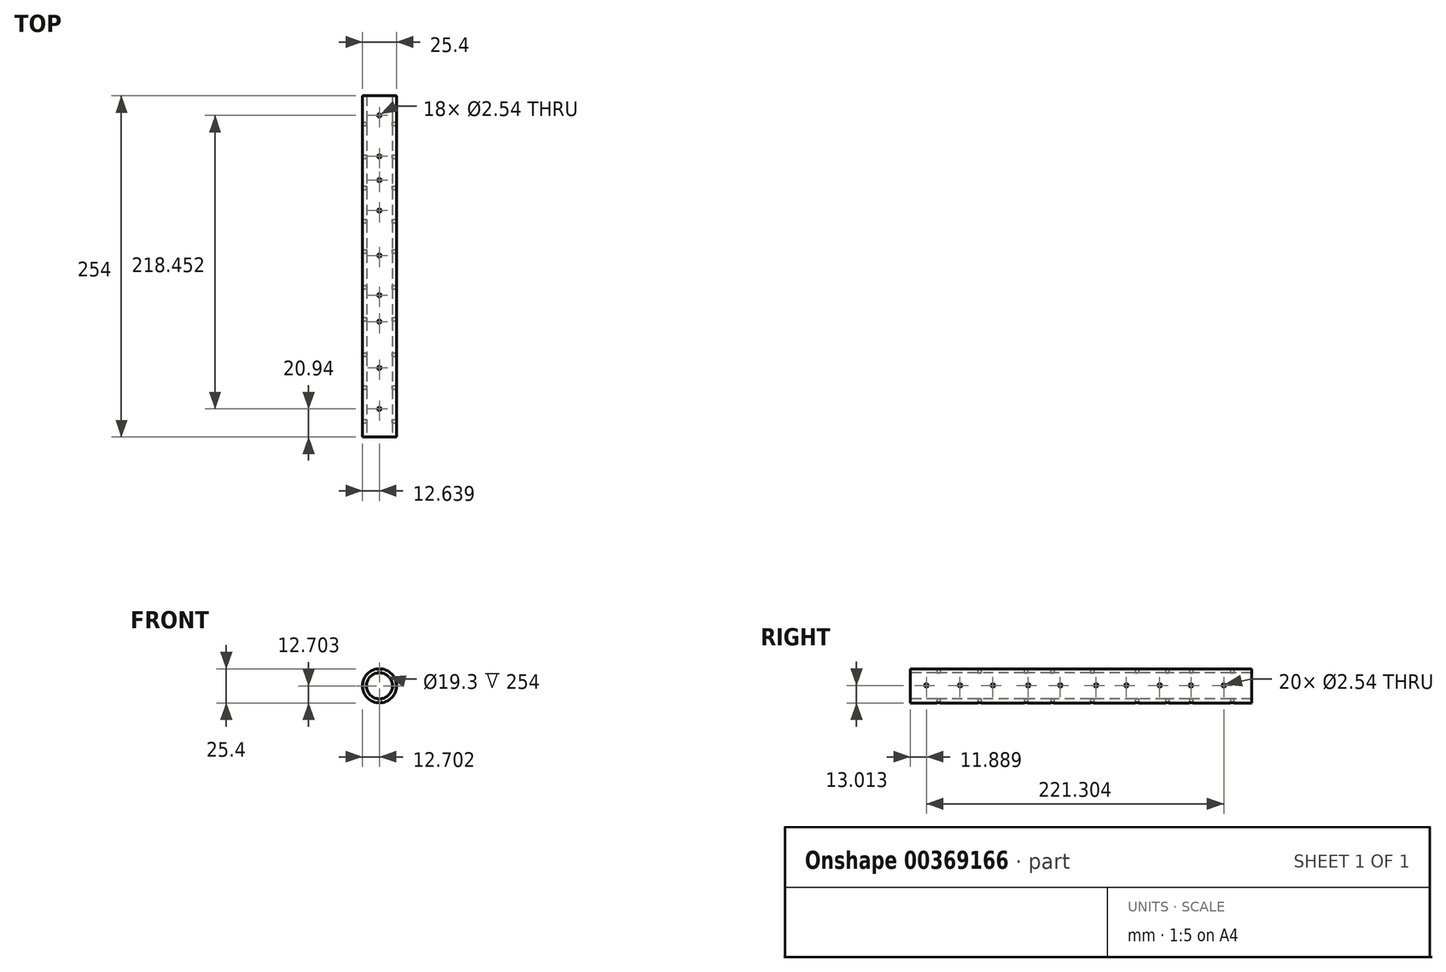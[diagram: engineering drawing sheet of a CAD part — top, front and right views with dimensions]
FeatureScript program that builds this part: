
annotation { "Feature Type Name" : "Feature", "Feature Type Description" : "" }
export const myFeature = defineFeature(function(context is Context, id is Id, definition is map)
    precondition{}
    {
        {
            var Q0;
            Q0=qCreatedBy(makeId("Front.planeOp"),FACE);
            var sketch = newSketch(context, id + "F0", { "sketchPlane" : qUnion([Q0])});
            skCircle(sketch, "E0", {"center": v(-39.62, 26.77) * mm, "radius": 12.7 * mm});
            skSolve(sketch);
        }
        {
            var Q0;
            Q0 = qSketchRegion(id + "F0", true);
            extrude(context, id + "F1", {"entities" : qUnion([Q0]), "depth" : 254 * mm});
        }
        {
            var Q0;
            Q0=makeQuery(id+"F1.opExtrude","CAP_FACE",FACE,{"disambiguationData":[OSD([sQuery(id+"F0.wireOp",EDGE,"E0")])],"isStart":false});
            var sketch = newSketch(context, id + "F2", { "sketchPlane" : qUnion([Q0])});
            skPoint(sketch, "E1", {"position": v(-39.62, 26.77) * mm});
            skSolve(sketch);
        }
        {
            var Q0;
            Q0=sQuery(id+"F2.wireOp",VERTEX,"E1");
            var Q1;
            Q1=makeQuery(id+"F1.opExtrude","SWEPT_BODY",BODY,{"disambiguationData":[OSD([sQuery(id+"F0.wireOp",EDGE,"E0")])]});
            hole(context, id + "F3", {"style" : HoleStyle.SIMPLE, "endStyle" : HoleEndStyle.THROUGH, "holeDiameter" : 19.3 * mm, "isTappedThrough" : true, "tappedDepth" : 12.7 * mm, "tapClearance" : 3, "locations" : qUnion([Q0]), "scope" : qUnion([Q1])});
        }
        {
            var Q0;
            Q0=qCreatedBy(makeId("Top.planeOp"),FACE);
            var sketch = newSketch(context, id + "F4", { "sketchPlane" : qUnion([Q0])});
            skPoint(sketch, "E2", {"position": v(-39.68, -233.06) * mm});
            skPoint(sketch, "E3", {"position": v(-39.68, -168.11) * mm});
            skPoint(sketch, "E4", {"position": v(-39.68, -85.46) * mm});
            skPoint(sketch, "E5", {"position": v(-39.68, -14.6) * mm});
            skPoint(sketch, "E6", {"position": v(-39.68, -45.11) * mm});
            skPoint(sketch, "E7", {"position": v(-39.68, -118.91) * mm});
            skPoint(sketch, "E8", {"position": v(-39.68, -202.56) * mm});
            skPoint(sketch, "E9", {"position": v(-39.68, -148.43) * mm});
            skPoint(sketch, "E10", {"position": v(-39.68, -62.83) * mm});
            skSolve(sketch);
        }
        {
            var Q0;
            Q0=sQuery(id+"F4.wireOp",VERTEX,"E2");
            var Q1;
            Q1=sQuery(id+"F4.wireOp",VERTEX,"E8");
            var Q2;
            Q2=sQuery(id+"F4.wireOp",VERTEX,"E3");
            var Q3;
            Q3=sQuery(id+"F4.wireOp",VERTEX,"E9");
            var Q4;
            Q4=sQuery(id+"F4.wireOp",VERTEX,"E7");
            var Q5;
            Q5=sQuery(id+"F4.wireOp",VERTEX,"E4");
            var Q6;
            Q6=sQuery(id+"F4.wireOp",VERTEX,"E10");
            var Q7;
            Q7=sQuery(id+"F4.wireOp",VERTEX,"E6");
            var Q8;
            Q8=sQuery(id+"F4.wireOp",VERTEX,"E5");
            var Q9;
            Q9=makeQuery(id+"F1.opExtrude","SWEPT_BODY",BODY,{"disambiguationData":[OSD([sQuery(id+"F0.wireOp",EDGE,"E0")])]});
            hole(context, id + "F5", {"style" : HoleStyle.SIMPLE, "endStyle" : HoleEndStyle.THROUGH, "oppositeDirection" : true, "holeDiameter" : 2.54 * mm, "isTappedThrough" : true, "tappedDepth" : 12.7 * mm, "tapClearance" : 3, "locations" : qUnion([Q0, Q1, Q2, Q3, Q4, Q5, Q6, Q7, Q8]), "scope" : qUnion([Q9])});
        }
        {
            var Q0;
            Q0=qCreatedBy(makeId("Right.planeOp"),FACE);
            var sketch = newSketch(context, id + "F6", { "sketchPlane" : qUnion([Q0])});
            skPoint(sketch, "E11", {"position": v(-242.11, 27.08) * mm});
            skPoint(sketch, "E12", {"position": v(-217.04, 27.08) * mm});
            skPoint(sketch, "E13", {"position": v(-192.59, 27.08) * mm});
            skPoint(sketch, "E14", {"position": v(-166.28, 27.08) * mm});
            skPoint(sketch, "E15", {"position": v(-142.45, 27.08) * mm});
            skPoint(sketch, "E16", {"position": v(-115.83, 27.08) * mm});
            skPoint(sketch, "E17", {"position": v(-93.23, 27.08) * mm});
            skPoint(sketch, "E18", {"position": v(-68.47, 27.08) * mm});
            skPoint(sketch, "E19", {"position": v(-45.26, 27.08) * mm});
            skPoint(sketch, "E20", {"position": v(-20.8, 27.08) * mm});
            skSolve(sketch);
        }
        {
            var Q0;
            Q0=sQuery(id+"F6.wireOp",VERTEX,"E13");
            var Q1;
            Q1=sQuery(id+"F6.wireOp",VERTEX,"E14");
            var Q2;
            Q2=sQuery(id+"F6.wireOp",VERTEX,"E15");
            var Q3;
            Q3=sQuery(id+"F6.wireOp",VERTEX,"E16");
            var Q4;
            Q4=sQuery(id+"F6.wireOp",VERTEX,"E17");
            var Q5;
            Q5=sQuery(id+"F6.wireOp",VERTEX,"E18");
            var Q6;
            Q6=sQuery(id+"F6.wireOp",VERTEX,"E19");
            var Q7;
            Q7=sQuery(id+"F6.wireOp",VERTEX,"E20");
            var Q8;
            Q8=sQuery(id+"F6.wireOp",VERTEX,"E12");
            var Q9;
            Q9=sQuery(id+"F6.wireOp",VERTEX,"E11");
            var Q10;
            Q10=makeQuery(id+"F1.opExtrude","SWEPT_BODY",BODY,{"disambiguationData":[OSD([sQuery(id+"F0.wireOp",EDGE,"E0")])]});
            hole(context, id + "F7", {"style" : HoleStyle.SIMPLE, "endStyle" : HoleEndStyle.THROUGH, "holeDiameter" : 2.54 * mm, "isTappedThrough" : true, "tappedDepth" : 12.7 * mm, "tapClearance" : 3, "locations" : qUnion([Q0, Q1, Q2, Q3, Q4, Q5, Q6, Q7, Q8, Q9]), "scope" : qUnion([Q10])});
        }
    });
